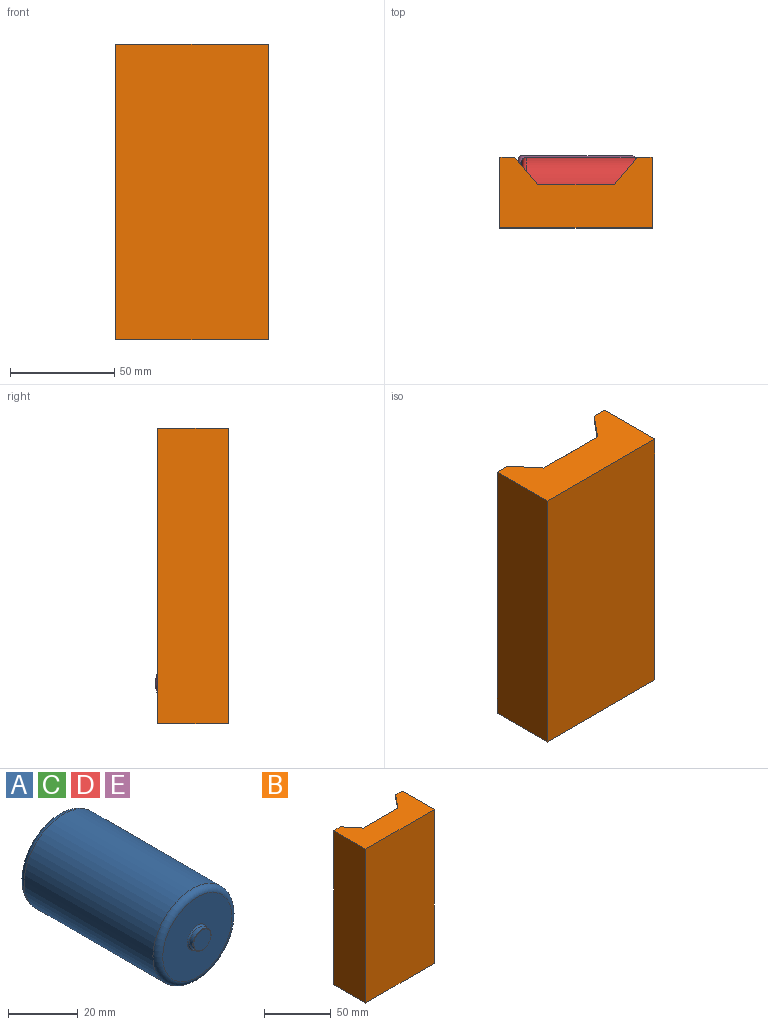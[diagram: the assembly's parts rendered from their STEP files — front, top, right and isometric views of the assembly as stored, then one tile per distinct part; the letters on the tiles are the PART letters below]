
ASSEMBLY  parts=5 mates=4
PART A: 9 faces, bbox 34.6x58.2x34.6 mm
  f0: cylinder r=16mm len=52.2mm, axis (0,1,0), area 5247.7mm2, adj f3,f4
  f1: plane 28x28mm, normal (0,-1,0), area 561.6mm2, adj f4,f8
  f2: plane 28x28mm, normal (0,1,0), area 615.8mm2, adj f3
  f3: torus R=14mm, axis (0,-1,0), area 301.5mm2, adj f0,f2
  f4: torus R=14mm, axis (0,-1,0), area 301.5mm2, adj f0,f1
  f5: cylinder r=3.65mm len=7.3mm, axis (0,1,0), area 29.8mm2, adj f7,f8
  f6: plane 6.9x6.9mm, normal (0,-1,0), area 37.4mm2, adj f7
  f7: torus R=3.45mm, axis (0,-1,0), area 7.1mm2, adj f5,f6
  f8: torus R=4.15mm, axis (0,-1,0), area 18.9mm2, adj f1,f5
PART B: 18 faces, bbox 73x34x141.5 mm
  f0: plane 141.5x7.11mm, normal (0,1,0), area 376.8mm2, adj f1,f2,f3,f6,f7,f10,f13,f16
  f1: plane 73x34mm, normal (0,0,1), area 1843.5mm2, adj f0,f4,f5,f7,f8,f15,f16,f17
  f2: plane 68x31.5mm, normal (0,0,-1), area 1503.5mm2, adj f0,f4,f9,f10,f11,f15,f16,f17
  f3: plane 68x31.5mm, normal (0,0,1), area 1503.5mm2, adj f0,f4,f9,f10,f11,f12,f13,f14
  f4: plane 141.5x7.11mm, normal (0,1,0), area 376.8mm2, adj f1,f2,f3,f5,f6,f9,f14,f15
  f5: plane 141.5x34mm, normal (-1,0,0), area 4811mm2, adj f1,f4,f6,f8
  f6: plane 73x34mm, normal (0,0,-1), area 1843.5mm2, adj f0,f4,f5,f7,f8,f12,f13,f14
  f7: plane 141.5x34mm, normal (1,0,0), area 4811mm2, adj f0,f1,f6,f8
  f8: plane 141.5x73mm, normal (0,-1,0), area 10329.5mm2, adj f1,f5,f6,f7
  f9: plane 136.5x31.5mm, normal (1,0,0), area 4299.8mm2, adj f2,f3,f4,f11
  f10: plane 136.5x31.5mm, normal (-1,0,0), area 4299.8mm2, adj f0,f2,f3,f11
  f11: plane 136.5x68mm, normal (0,1,0), area 9282mm2, adj f2,f3,f9,f10
  f12: plane 36.62x2.5mm, normal (0,1,0), area 91.5mm2, adj f3,f6,f13,f14
  f13: plane 13.39x11.08mm, normal (-0.77,0.64,0), area 43.4mm2, adj f0,f3,f6,f12
  f14: plane 13.39x11.08mm, normal (0.77,0.64,0), area 43.4mm2, adj f3,f4,f6,f12
  f15: plane 13.39x11.08mm, normal (0.77,0.64,0), area 43.4mm2, adj f1,f2,f4,f17
  f16: plane 13.39x11.08mm, normal (-0.77,0.64,0), area 43.4mm2, adj f0,f1,f2,f17
  f17: plane 36.62x2.5mm, normal (0,1,0), area 91.5mm2, adj f1,f2,f15,f16
PART C: same geometry as A
PART D: same geometry as A
PART E: same geometry as A
PLACE A rot(axis=(-0.58,0.58,0.58),120deg) t=(-55.32,-14.19,21.77)mm
PLACE B t=(-28.93,2.41,4.59)mm
PLACE C rot(axis=(-0.58,-0.58,-0.58),120deg) t=(1.41,-14.95,-12.19)mm
PLACE D rot(axis=(-0.58,-0.58,-0.58),120deg) t=(1.42,-13.86,55.48)mm
PLACE E rot(axis=(-0.58,0.58,0.58),120deg) t=(-56.59,-12.63,-46.84)mm
MATE parallel A.f0 <-> B.f9  axis (-1,0,0) through (-55.32,-14.19,21.77)mm
MATE parallel D.f0 <-> B.f10  axis (-1,0,0) through (-0.58,-13.86,55.48)mm
MATE parallel C.f0 <-> B.f10  axis (1,0,0) through (1.41,-14.95,-12.19)mm
MATE parallel E.f0 <-> B.f9  axis (-1,0,0) through (-56.59,-12.63,-46.84)mm
